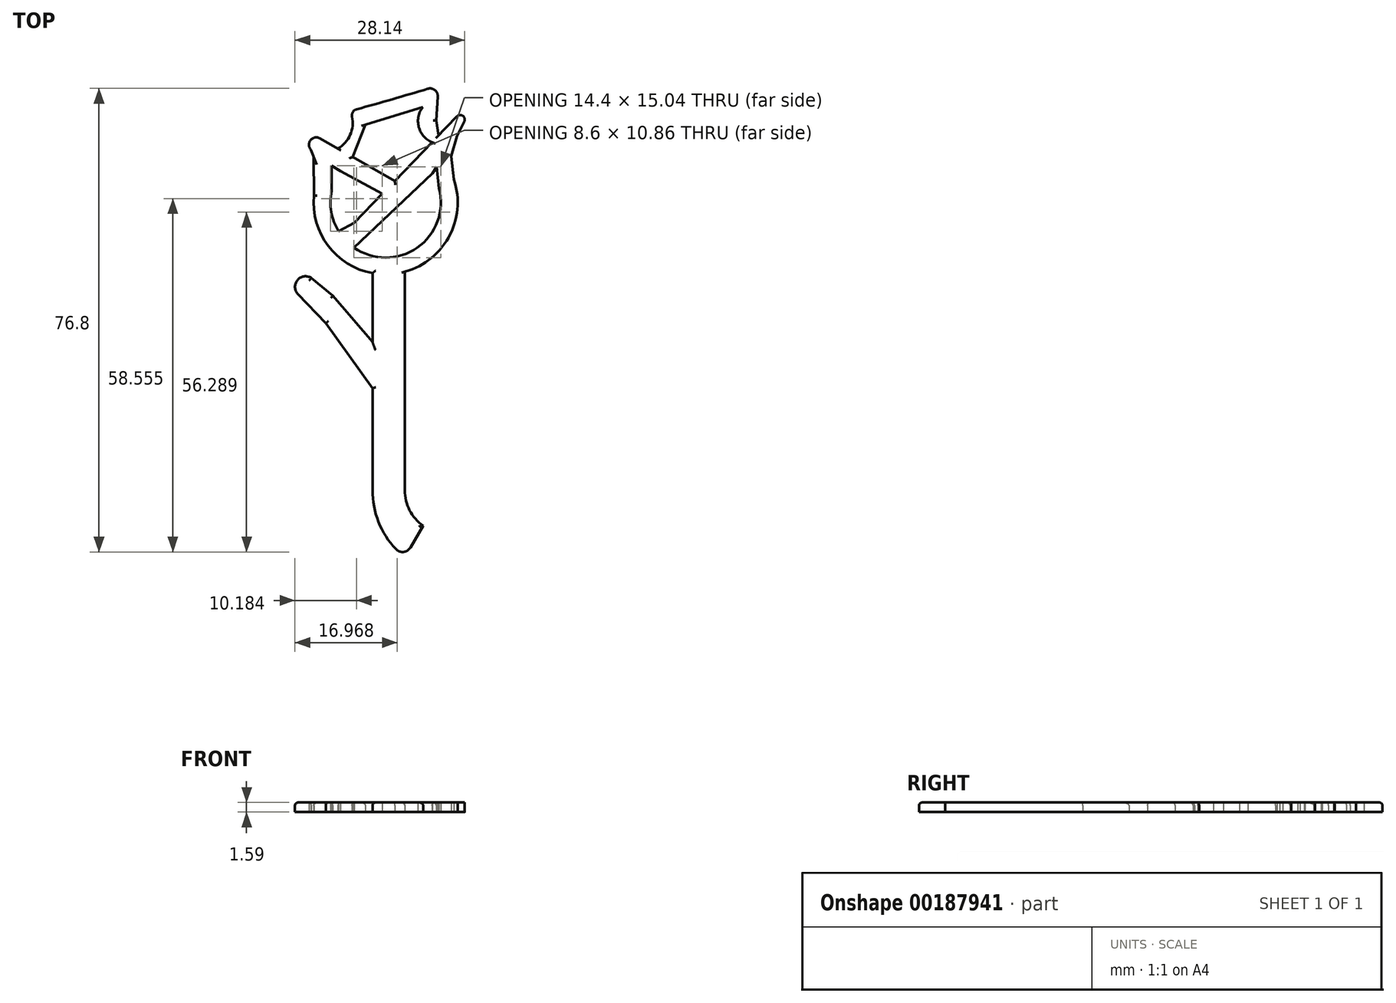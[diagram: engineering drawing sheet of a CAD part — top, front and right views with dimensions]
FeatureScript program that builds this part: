
annotation { "Feature Type Name" : "Feature", "Feature Type Description" : "" }
export const myFeature = defineFeature(function(context is Context, id is Id, definition is map)
    precondition{}
    {
        {
            var Q0;
            Q0=qCreatedBy(makeId("Top.planeOp"),FACE);
            var sketch = newSketch(context, id + "F0", { "sketchPlane" : qUnion([Q0])});
            skLineSegment(sketch, "E0", {"start": v(0, 36.18) * mm, "end": v(0, 0) * mm});
            skLineSegment(sketch, "E1", {"start": v(-5.35, 35.96) * mm, "end": v(-5.35, 24.57) * mm});
            skLineSegment(sketch, "E2", {"start": v(3.04, -5.9) * mm, "end": v(0.95, -9.47) * mm});
            skArc(sketch, "E3", {"start": v(0, 0) * mm, "mid": v(0.8, -3.32) * mm, "end": v(3.04, -5.9) * mm});
            skArc(sketch, "E4", {"start": v(-5.35, 0) * mm, "mid": v(-4.34, -5.25) * mm, "end": v(-1.47, -9.75) * mm});
            skLineSegment(sketch, "E5", {"start": v(-5.35, 16.88) * mm, "end": v(-13.1, 27.65) * mm});
            skLineSegment(sketch, "E6", {"start": v(-13.1, 27.65) * mm, "end": v(-17.7, 32.47) * mm});
            skArc(sketch, "E7", {"start": v(-15.49, 35.18) * mm, "mid": v(-17.8, 34.8) * mm, "end": v(-17.7, 32.47) * mm});
            skArc(sketch, "E8", {"start": v(-15.03, 48.83) * mm, "mid": v(-12.7, 40.51) * mm, "end": v(-5.35, 35.96) * mm});
            skLineSegment(sketch, "E9", {"start": v(7.72, 55.37) * mm, "end": v(8.65, 58.65) * mm});
            skLineSegment(sketch, "E10", {"start": v(8.65, 58.65) * mm, "end": v(9.87, 61.08) * mm});
            skLineSegment(sketch, "E11", {"start": v(-15.08, 55.25) * mm, "end": v(-15.53, 56.39) * mm});
            skLineSegment(sketch, "E12", {"start": v(-8.37, 44.27) * mm, "end": v(-3.7, 49.11) * mm});
            skLineSegment(sketch, "E13", {"start": v(-10.68, 52.89) * mm, "end": v(-3.7, 49.11) * mm});
            skLineSegment(sketch, "E14", {"start": v(-1.65, 51.25) * mm, "end": v(-8.6, 55.2) * mm});
            skLineSegment(sketch, "E15", {"start": v(-8.42, 40.2) * mm, "end": v(4.6, 52.52) * mm});
            skPoint(sketch, "E15.startSnap0", {"position": v(-8.42, 51.67) * mm});
            skArc(sketch, "E16", {"start": v(-14.04, 58.3) * mm, "mid": v(-15.61, 57.99) * mm, "end": v(-15.53, 56.39) * mm});
            skLineSegment(sketch, "E17", {"start": v(-8.6, 55.2) * mm, "end": v(-6.54, 60.58) * mm});
            skLineSegment(sketch, "E18", {"start": v(-6.54, 60.58) * mm, "end": v(2.98, 63.5) * mm});
            skArc(sketch, "E19", {"start": v(2.98, 63.5) * mm, "mid": v(2.32, 60.2) * mm, "end": v(4.51, 57.64) * mm});
            skLineSegment(sketch, "E20", {"start": v(5.2, 61.26) * mm, "end": v(5.46, 65.22) * mm});
            skArc(sketch, "E21", {"start": v(-11.07, 56.62) * mm, "mid": v(-9.03, 58.89) * mm, "end": v(-8.72, 61.92) * mm});
            skArc(sketch, "E22", {"start": v(-8, 63.12) * mm, "mid": v(-2.07, 64.78) * mm, "end": v(3.83, 66.52) * mm});
            skArc(sketch, "E23", {"start": v(9.87, 61.08) * mm, "mid": v(9.63, 62.03) * mm, "end": v(8.65, 61.94) * mm});
            skArc(sketch, "E24", {"start": v(-12.11, 49.56) * mm, "mid": v(-12.17, 46.12) * mm, "end": v(-10.95, 42.9) * mm});
            skLineSegment(sketch, "E25.trimOffspring", {"start": v(-11.07, 56.62) * mm, "end": v(-14.04, 58.3) * mm});
            skPoint(sketch, "E26.orphan", {"position": v(-13.14, 54.22) * mm});
            skLineSegment(sketch, "E27.trimOffspring", {"start": v(5.6, 58.77) * mm, "end": v(8.65, 61.94) * mm});
            skLineSegment(sketch, "E28", {"start": v(7.72, 55.37) * mm, "end": v(8.16, 51.46) * mm});
            skLineSegment(sketch, "E29", {"start": v(5.68, 50.05) * mm, "end": v(5.28, 53.58) * mm});
            skLineSegment(sketch, "E30", {"start": v(5.28, 53.58) * mm, "end": v(4.6, 52.52) * mm});
            skPoint(sketch, "E31.orphan", {"position": v(7.21, 53.58) * mm});
            skLineSegment(sketch, "E32", {"start": v(-15.08, 55.25) * mm, "end": v(-15.03, 48.83) * mm});
            skLineSegment(sketch, "E33", {"start": v(-12.11, 49.56) * mm, "end": v(-12.11, 53.75) * mm});
            skLineSegment(sketch, "E34", {"start": v(-12.11, 53.75) * mm, "end": v(-10.68, 52.89) * mm});
            skPoint(sketch, "E35.orphan", {"position": v(-14.04, 52.59) * mm});
            skPoint(sketch, "E36.visualSharp", {"position": v(0, -11.1) * mm});
            skArc(sketch, "E36.filletArc", {"start": v(-1.47, -9.75) * mm, "mid": v(-0.19, -10.22) * mm, "end": v(0.95, -9.47) * mm});
            skPoint(sketch, "E37.visualSharp", {"position": v(-9.02, 62.84) * mm});
            skArc(sketch, "E37.filletArc", {"start": v(-8, 63.12) * mm, "mid": v(-8.6, 62.66) * mm, "end": v(-8.72, 61.92) * mm});
            skPoint(sketch, "E38.visualSharp", {"position": v(5.58, 67.05) * mm});
            skArc(sketch, "E38.filletArc", {"start": v(5.46, 65.22) * mm, "mid": v(4.99, 66.3) * mm, "end": v(3.83, 66.52) * mm});
            skLineSegment(sketch, "E39", {"start": v(5.6, 58.77) * mm, "end": v(5.2, 61.26) * mm});
            skLineSegment(sketch, "E40", {"start": v(-10.95, 42.9) * mm, "end": v(-8.37, 44.27) * mm});
            skArc(sketch, "E41.trimOffspring", {"start": v(-8.42, 40.2) * mm, "mid": v(2.08, 40.18) * mm, "end": v(5.68, 50.05) * mm});
            skArc(sketch, "E42.trimOffspring", {"start": v(0, 36.18) * mm, "mid": v(7.37, 42.07) * mm, "end": v(8.16, 51.46) * mm});
            skLineSegment(sketch, "E43.trimOffspring", {"start": v(-1.65, 51.25) * mm, "end": v(4.51, 57.64) * mm});
            skLineSegment(sketch, "E44.trimOffspring", {"start": v(-5.35, 16.88) * mm, "end": v(-5.35, 0) * mm});
            skLineSegment(sketch, "E45", {"start": v(-15.49, 35.18) * mm, "end": v(-11.9, 32.2) * mm});
            skLineSegment(sketch, "E46", {"start": v(-11.9, 32.2) * mm, "end": v(-5.35, 24.57) * mm});
            skSolve(sketch);
        }
        {
            var Q0;
            Q0=makeQuery(id+"F0.imprint","IMPRINT",FACE,{"disambiguationData":[TD([[makeQuery(id+"F0.imprint","IMPRINT",EDGE,{"derivedFrom":sQuery(id+"F0.wireOp",EDGE,"E0")}),-1.0]])]});
            extrude(context, id + "F1", {"entities" : qUnion([Q0]), "depth" : 1.59 * mm});
        }
        {
            var Q0;
            Q0=makeQuery(id+"F1.opExtrude","CAP_EDGE",EDGE,{"disambiguationData":[OSD([sQuery(id+"F0.wireOp",EDGE,"E17")])],"isStart":false});
            var Q1;
            Q1=makeQuery(id+"F1.opExtrude","CAP_EDGE",EDGE,{"disambiguationData":[OSD([sQuery(id+"F0.wireOp",EDGE,"E14")])],"isStart":false});
            var Q2;
            Q2=makeQuery(id+"F1.opExtrude","CAP_EDGE",EDGE,{"disambiguationData":[OSD([sQuery(id+"F0.wireOp",EDGE,"E43.trimOffspring")])],"isStart":false});
            var Q3;
            Q3=makeQuery(id+"F1.opExtrude","CAP_EDGE",EDGE,{"disambiguationData":[OSD([sQuery(id+"F0.wireOp",EDGE,"E21")])],"isStart":false});
            var Q4;
            Q4=makeQuery(id+"F1.opExtrude","CAP_EDGE",EDGE,{"disambiguationData":[OSD([sQuery(id+"F0.wireOp",EDGE,"E39")])],"isStart":false});
            var Q5;
            Q5=makeQuery(id+"F1.opExtrude","CAP_EDGE",EDGE,{"disambiguationData":[OSD([sQuery(id+"F0.wireOp",EDGE,"E32")])],"isStart":false});
            var Q6;
            Q6=makeQuery(id+"F1.opExtrude","CAP_EDGE",EDGE,{"disambiguationData":[OSD([sQuery(id+"F0.wireOp",EDGE,"E8")])],"isStart":false});
            var Q7;
            Q7=makeQuery(id+"F1.opExtrude","CAP_EDGE",EDGE,{"disambiguationData":[OSD([sQuery(id+"F0.wireOp",EDGE,"E1")])],"isStart":false});
            var Q8;
            Q8=makeQuery(id+"F1.opExtrude","CAP_EDGE",EDGE,{"disambiguationData":[OSD([sQuery(id+"F0.wireOp",EDGE,"E46")])],"isStart":false});
            var Q9;
            Q9=makeQuery(id+"F1.opExtrude","CAP_EDGE",EDGE,{"disambiguationData":[OSD([sQuery(id+"F0.wireOp",EDGE,"E45")])],"isStart":false});
            var Q10;
            Q10=makeQuery(id+"F1.opExtrude","CAP_EDGE",EDGE,{"disambiguationData":[OSD([sQuery(id+"F0.wireOp",EDGE,"E7")])],"isStart":false});
            var Q11;
            Q11=makeQuery(id+"F1.opExtrude","CAP_EDGE",EDGE,{"disambiguationData":[OSD([sQuery(id+"F0.wireOp",EDGE,"E6")])],"isStart":false});
            var Q12;
            Q12=makeQuery(id+"F1.opExtrude","CAP_EDGE",EDGE,{"disambiguationData":[OSD([sQuery(id+"F0.wireOp",EDGE,"E5")])],"isStart":false});
            var Q13;
            Q13=makeQuery(id+"F1.opExtrude","CAP_EDGE",EDGE,{"disambiguationData":[OSD([sQuery(id+"F0.wireOp",EDGE,"E44.trimOffspring")])],"isStart":false});
            var Q14;
            Q14=makeQuery(id+"F1.opExtrude","CAP_EDGE",EDGE,{"disambiguationData":[OSD([sQuery(id+"F0.wireOp",EDGE,"E3")])],"isStart":false});
            fillet(context, id + "F2", {"entities" : qUnion([Q0, Q1, Q2, Q3, Q4, Q5, Q6, Q7, Q8, Q9, Q10, Q11, Q12, Q13, Q14]), "radius" : 0.5 * mm, "tangentPropagation" : true, "allowEdgeOverflow" : false});
        }
    });
